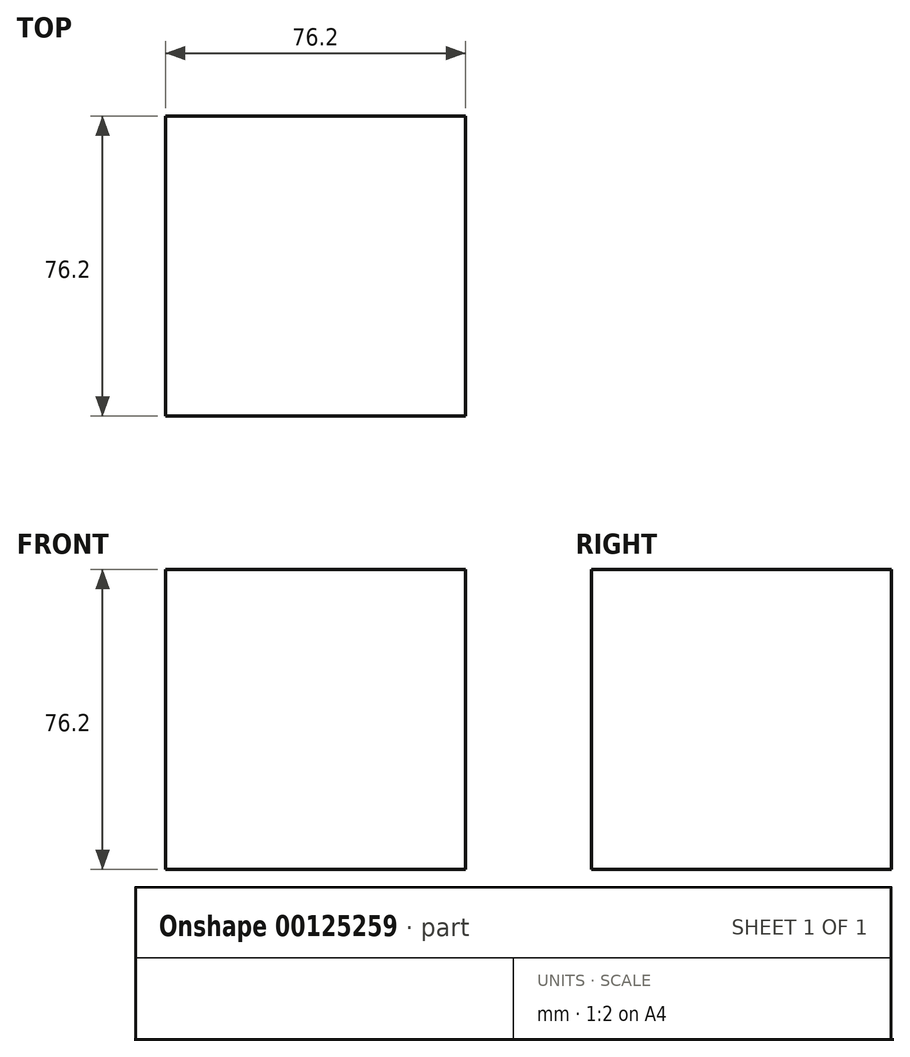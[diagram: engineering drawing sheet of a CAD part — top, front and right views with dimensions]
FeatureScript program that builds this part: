
annotation { "Feature Type Name" : "Feature", "Feature Type Description" : "" }
export const myFeature = defineFeature(function(context is Context, id is Id, definition is map)
    precondition{}
    {
        {
            var Q0;
            Q0=qCreatedBy(makeId("Front.planeOp"),FACE);
            var sketch = newSketch(context, id + "F0", { "sketchPlane" : qUnion([Q0])});
            skLineSegment(sketch, "E0.bottom", {"start": v(38.1, 38.1) * mm, "end": v(-38.1, 38.1) * mm});
            skLineSegment(sketch, "E0.top", {"start": v(38.1, -38.1) * mm, "end": v(-38.1, -38.1) * mm});
            skLineSegment(sketch, "E0.left", {"start": v(38.1, 38.1) * mm, "end": v(38.1, -38.1) * mm});
            skLineSegment(sketch, "E0.right", {"start": v(-38.1, 38.1) * mm, "end": v(-38.1, -38.1) * mm});
            skPoint(sketch, "E0.middle", {"position": v(0, 0) * mm});
            skSolve(sketch);
        }
        {
            var Q0;
            Q0=makeQuery(id+"F0.imprint","IMPRINT",FACE,{"disambiguationData":[TD([[makeQuery(id+"F0.imprint","IMPRINT",EDGE,{"derivedFrom":sQuery(id+"F0.wireOp",EDGE,"E0.bottom")}),1.0]])]});
            extrude(context, id + "F1", {"entities" : qUnion([Q0]), "endBound" : BoundingType.SYMMETRIC, "depth" : 76.2 * mm});
        }
    });
